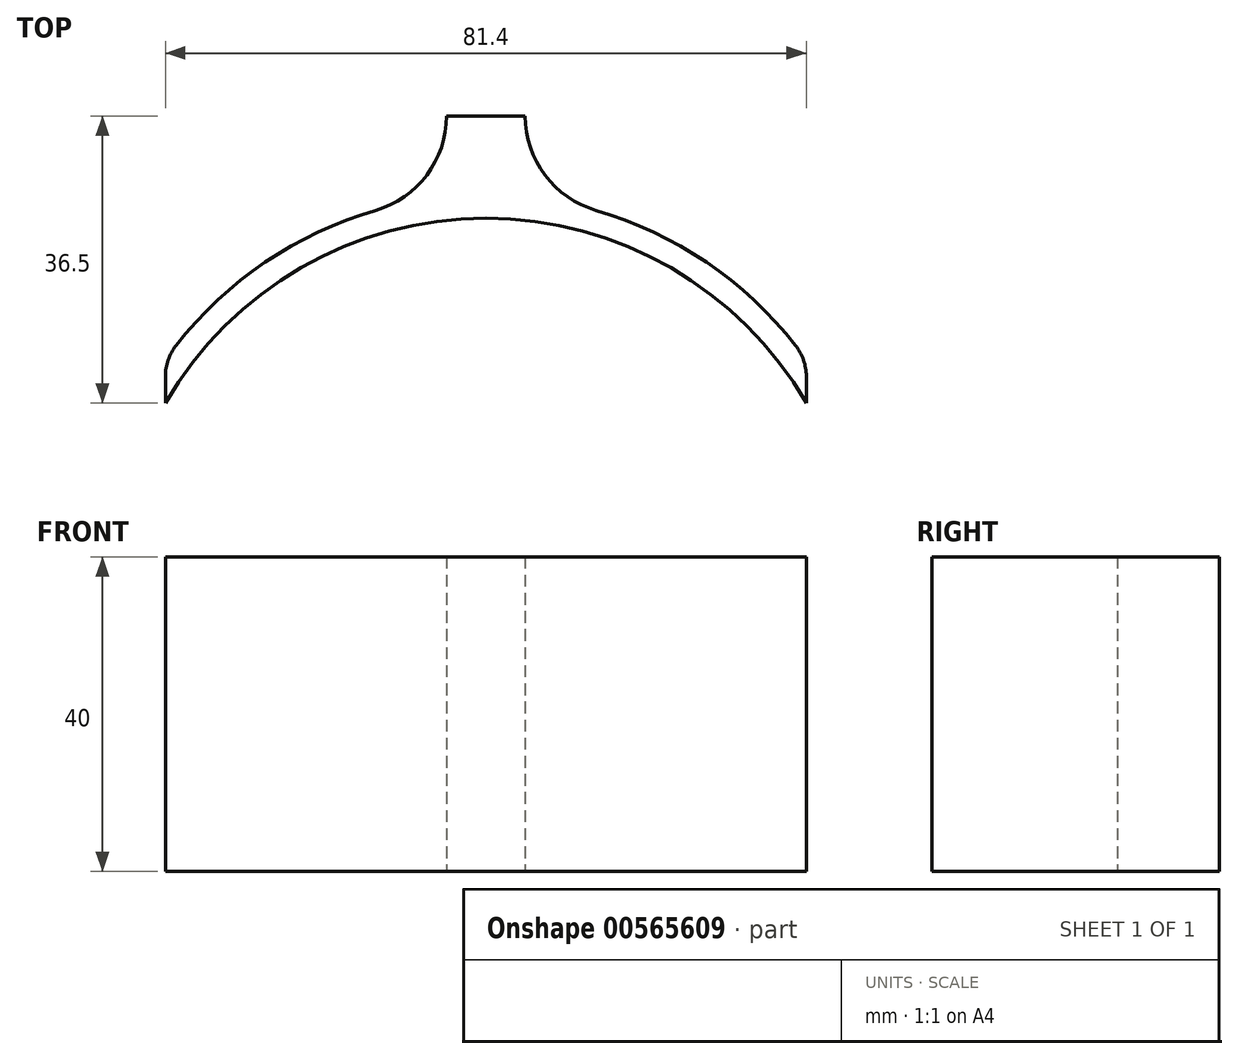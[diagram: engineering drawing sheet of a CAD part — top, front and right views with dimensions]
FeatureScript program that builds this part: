
annotation { "Feature Type Name" : "Feature", "Feature Type Description" : "" }
export const myFeature = defineFeature(function(context is Context, id is Id, definition is map)
    precondition{}
    {
        {
            var Q0;
            Q0=qCreatedBy(makeId("Top.planeOp"),FACE);
            var sketch = newSketch(context, id + "F0", { "sketchPlane" : qUnion([Q0])});
            skArc(sketch, "E0", {"start": v(39.35, 30.85) * mm, "mid": v(0, 50) * mm, "end": v(-39.35, 30.85) * mm});
            skLineSegment(sketch, "E1", {"start": v(0, 0) * mm, "end": v(-40.7, 23.5) * mm, "construction": true});
            skLineSegment(sketch, "E2", {"start": v(0, 0) * mm, "end": v(40.7, 23.5) * mm, "construction": true});
            skLineSegment(sketch, "E3", {"start": v(0, 0) * mm, "end": v(0, 60) * mm, "construction": true});
            skLineSegment(sketch, "E4.bottom", {"start": v(-5, 60) * mm, "end": v(5, 60) * mm});
            skLineSegment(sketch, "E4.top", {"start": v(-5, 49.75) * mm, "end": v(5, 49.75) * mm});
            skLineSegment(sketch, "E4.left", {"start": v(-5, 60) * mm, "end": v(-5, 49.75) * mm});
            skLineSegment(sketch, "E4.right", {"start": v(5, 60) * mm, "end": v(5, 49.75) * mm});
            skArc(sketch, "E5", {"start": v(-14, 48) * mm, "mid": v(-7.5, 52.5) * mm, "end": v(-5, 60) * mm});
            skArc(sketch, "E6", {"start": v(5, 60) * mm, "mid": v(7.5, 52.5) * mm, "end": v(14, 48) * mm});
            skArc(sketch, "E7", {"start": v(40.7, 23.5) * mm, "mid": v(0, 47) * mm, "end": v(-40.7, 23.5) * mm});
            skLineSegment(sketch, "E8", {"start": v(40.7, 23.5) * mm, "end": v(40.7, 26.93) * mm});
            skLineSegment(sketch, "E9", {"start": v(-40.7, 26.93) * mm, "end": v(-40.7, 23.5) * mm});
            skPoint(sketch, "E10.visualSharp", {"position": v(-40.7, 29.04) * mm});
            skArc(sketch, "E10.filletArc", {"start": v(-39.35, 30.85) * mm, "mid": v(-40.36, 29) * mm, "end": v(-40.7, 26.93) * mm});
            skPoint(sketch, "E11.visualSharp", {"position": v(40.7, 29.04) * mm});
            skArc(sketch, "E11.filletArc", {"start": v(40.7, 26.93) * mm, "mid": v(40.36, 29) * mm, "end": v(39.35, 30.85) * mm});
            skSolve(sketch);
        }
        {
            var Q0;
            Q0=makeQuery(id+"F0.imprint","IMPRINT",FACE,{"disambiguationData":[TD([[makeQuery(id+"F0.imprint","IMPRINT",EDGE,{"derivedFrom":sQuery(id+"F0.wireOp",EDGE,"E4.bottom")}),-1.0]])]});
            var Q1;
            {var subQ0=sQuery(id+"F0.wireOp",EDGE,"E4.left");Q1=makeQuery(id+"F0.imprint","IMPRINT",FACE,{"disambiguationData":[TD([[makeQuery(id+"F0.imprint","IMPRINT",EDGE,{"derivedFrom":subQ0}),-1.0]])]});}
            var Q2;
            {var subQ0=sQuery(id+"F0.wireOp",EDGE,"E4.right");Q2=makeQuery(id+"F0.imprint","IMPRINT",FACE,{"disambiguationData":[TD([[makeQuery(id+"F0.imprint","IMPRINT",EDGE,{"derivedFrom":subQ0}),1.0]])]});}
            var Q3;
            {var subQ4=sQuery(id+"F0.wireOp",EDGE,"E4.top");Q3=makeQuery(id+"F0.imprint","IMPRINT",FACE,{"disambiguationData":[TD([[makeQuery(id+"F0.imprint","IMPRINT",EDGE,{"derivedFrom":subQ4}),-1.0]])]});}
            var Q4;
            {var subQ0=sQuery(id+"F0.wireOp",EDGE,"E4.top");Q4=makeQuery(id+"F0.imprint","IMPRINT",FACE,{"disambiguationData":[TD([[makeQuery(id+"F0.imprint","IMPRINT",EDGE,{"derivedFrom":subQ0}),1.0]])]});}
            extrude(context, id + "F1", {"entities" : qUnion([Q0, Q1, Q2, Q3, Q4]), "depth" : 40 * mm, "offsetDistance" : 25 * mm});
        }
    });
